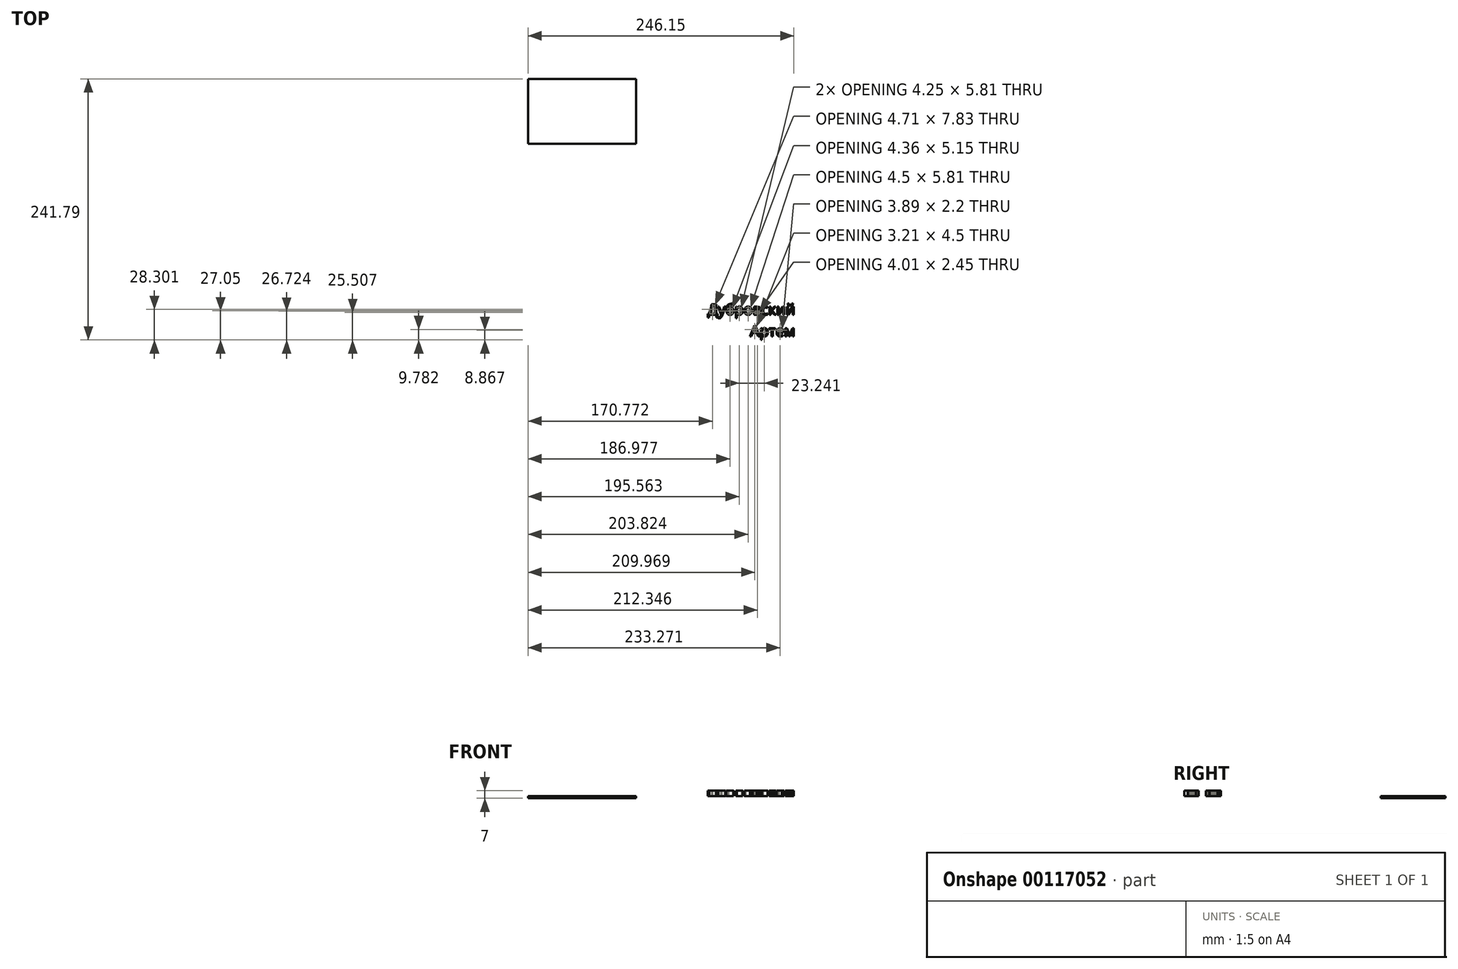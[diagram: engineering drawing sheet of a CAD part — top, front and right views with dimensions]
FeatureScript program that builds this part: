
annotation { "Feature Type Name" : "Feature", "Feature Type Description" : "" }
export const myFeature = defineFeature(function(context is Context, id is Id, definition is map)
    precondition{}
    {
        {
            var Q0;
            Q0=qCreatedBy(makeId("Top.planeOp"),FACE);
            var sketch = newSketch(context, id + "F0", { "sketchPlane" : qUnion([Q0])});
            skText(sketch, "E0", { "text": "Дубровский", "fontName": "OpenSans-Regular.ttf"});
            skText(sketch, "E1", { "text": "Артем", "fontName": "OpenSans-Regular.ttf"});
            skLineSegment(sketch, "E2.bottom", {"start": v(-229.37, 243.55) * mm, "end": v(-129.37, 243.55) * mm});
            skLineSegment(sketch, "E2.right", {"start": v(-129.37, 243.55) * mm, "end": v(-129.37, 183.55) * mm});
            skLineSegment(sketch, "E3", {"start": v(-129.37, 243.55) * mm, "end": v(-137.37, 243.55) * mm});
            skLineSegment(sketch, "E4", {"start": v(34.34, -60.68) * mm, "end": v(34.34, -44.68) * mm});
            skPoint(sketch, "E5.endSnap0", {"position": v(3.34, 24.32) * mm});
            skLineSegment(sketch, "E6", {"start": v(3.34, -75.06) * mm, "end": v(3.34, -60.68) * mm});
            skPoint(sketch, "E7.center", {"position": v(3.34, 1.57) * mm});
            const initialGuessF0  = {"E0": [-0.06302, 0.0251, 1, 0, 0.01], "E1": [-0.0238, 0.0051, 1, 0, 0.01]};
            skSetInitialGuess(sketch, initialGuessF0);
            skSolve(sketch);
        }
        {
            var Q0;
            Q0 = qSketchRegion(id + "F0", true);
            extrude(context, id + "F1", {"entities" : qUnion([Q0]), "depth" : 5 * mm});
        }
        {
            var Q0;
            Q0=qCreatedBy(makeId("Top.planeOp"),FACE);
            var sketch = newSketch(context, id + "F2", { "sketchPlane" : qUnion([Q0])});
            skPoint(sketch, "E8", {"position": v(-229.37, 243.55) * mm});
            skLineSegment(sketch, "E9", {"start": v(-229.37, 243.55) * mm, "end": v(-129.37, 243.55) * mm});
            skLineSegment(sketch, "E10", {"start": v(-129.37, 243.55) * mm, "end": v(-129.37, 183.55) * mm});
            skLineSegment(sketch, "E11", {"start": v(-129.37, 183.55) * mm, "end": v(-229.37, 183.55) * mm});
            skLineSegment(sketch, "E12", {"start": v(-229.37, 183.55) * mm, "end": v(-229.37, 243.55) * mm});
            skPoint(sketch, "E13", {"position": v(17.69, 35.1) * mm});
            skPoint(sketch, "E14", {"position": v(-137.37, 243.55) * mm});
            skSolve(sketch);
        }
        {
            var Q0;
            Q0 = qSketchRegion(id + "F2", true);
            extrude(context, id + "F3", {"entities" : qUnion([Q0]), "oppositeDirection" : true, "depth" : 2 * mm});
        }
    });
